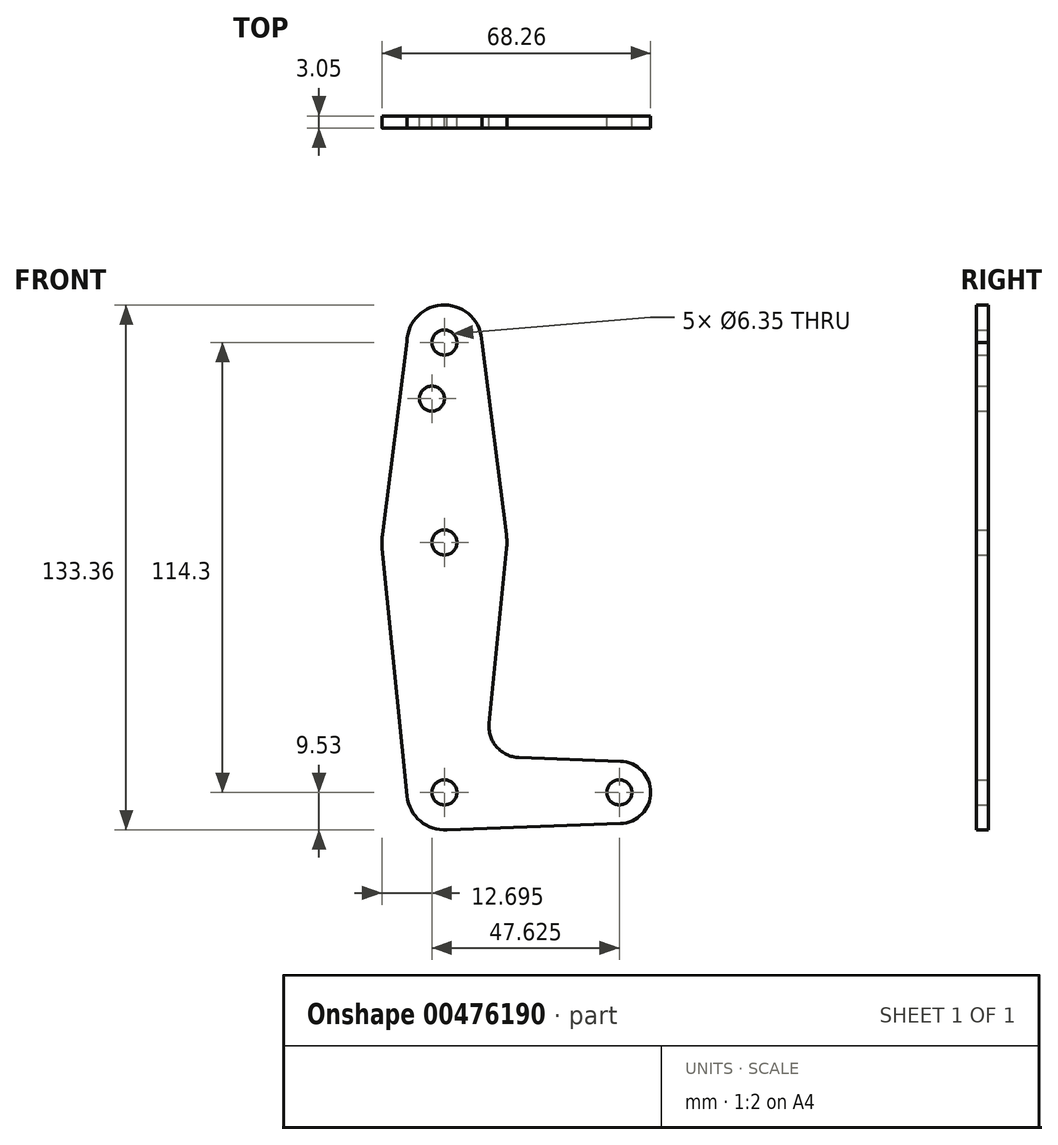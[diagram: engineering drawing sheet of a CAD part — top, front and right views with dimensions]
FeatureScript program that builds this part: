
annotation { "Feature Type Name" : "Feature", "Feature Type Description" : "" }
export const myFeature = defineFeature(function(context is Context, id is Id, definition is map)
    precondition{}
    {
        {
            var Q0;
            Q0=qCreatedBy(makeId("Front.planeOp"),FACE);
            var sketch = newSketch(context, id + "F0", { "sketchPlane" : qUnion([Q0])});
            skLineSegment(sketch, "E0", {"start": v(0, 0) * mm, "end": v(0, 63.5) * mm, "construction": true});
            skLineSegment(sketch, "E1", {"start": v(0, 63.5) * mm, "end": v(0, 114.3) * mm, "construction": true});
            skLineSegment(sketch, "E2", {"start": v(0, 0) * mm, "end": v(44.45, 0) * mm, "construction": true});
            skCircle(sketch, "E3", {"center": v(44.45, 0) * mm, "radius": 7.94 * mm});
            skCircle(sketch, "E4", {"center": v(0, 0) * mm, "radius": 9.53 * mm});
            skCircle(sketch, "E5", {"center": v(0, 63.5) * mm, "radius": 15.88 * mm});
            skCircle(sketch, "E6", {"center": v(0, 114.3) * mm, "radius": 9.53 * mm});
            skLineSegment(sketch, "E7", {"start": v(44.73, 7.93) * mm, "end": v(18.95, 8.85) * mm});
            skLineSegment(sketch, "E8", {"start": v(-0.03, -9.52) * mm, "end": v(44.73, -7.93) * mm});
            skLineSegment(sketch, "E9", {"start": v(9.52, 114.3) * mm, "end": v(15.75, 65.5) * mm});
            skLineSegment(sketch, "E10", {"start": v(-9.52, 114.5) * mm, "end": v(-15.75, 65.5) * mm});
            skLineSegment(sketch, "E11", {"start": v(15.8, 61.91) * mm, "end": v(11.34, 17.58) * mm});
            skLineSegment(sketch, "E12", {"start": v(-15.8, 61.91) * mm, "end": v(-9.48, -0.95) * mm});
            skArc(sketch, "E13.filletArc", {"start": v(11.34, 17.58) * mm, "mid": v(13.26, 11.57) * mm, "end": v(18.95, 8.85) * mm});
            skCircle(sketch, "E14", {"center": v(0, 114.3) * mm, "radius": 3.18 * mm});
            skCircle(sketch, "E15", {"center": v(0, 63.5) * mm, "radius": 3.18 * mm});
            skCircle(sketch, "E16", {"center": v(0, 0) * mm, "radius": 3.18 * mm});
            skCircle(sketch, "E17", {"center": v(44.45, 0) * mm, "radius": 3.18 * mm});
            skCircle(sketch, "E18", {"center": v(-3.18, 100.03) * mm, "radius": 3.18 * mm});
            skSolve(sketch);
        }
        {
            var Q0;
            Q0 = qSketchRegion(id + "F0", true);
            extrude(context, id + "F1", {"entities" : qUnion([Q0]), "depth" : 3.05 * mm});
        }
    });
